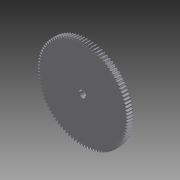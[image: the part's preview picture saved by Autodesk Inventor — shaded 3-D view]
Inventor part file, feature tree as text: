
AUTODESK INVENTOR PART (.ipt)
format: ipt  version: 2013 SP2 (Build 170200200, 200)  size: 855,040 bytes
history: native  units: in
note: dims shown in document units (in); Inventor stores cm internally (conversion verified against a paired STEP export)
features: extrude x4, sketch x4, imported_body x1
ambient origin geometry x8: Origin, YZ Plane, XZ Plane, XY Plane, X Axis, Y Axis, Z Axis, Center Point
bodies: Solid1 (feature_tree)
feature tree (9):
  imported_body  "Base1"
  extrude  "Extrusion2"  Depth=0.66in TaperAngle=0.0deg
  extrude  "Extrusion3"  Depth=0.41in TaperAngle=0.0deg
  extrude  "Extrusion4"  Depth=0.171in
  extrude  "Extrusion5"  Depth=1.0in TaperAngle=0.0deg
  sketch  "Sketch2"  dims[d6=0.215in d7=0.66in d8=0.0in]
  sketch  "Sketch3"  dims[d9=0.7in d11=0.41in d12=0.0in]
  sketch  "Sketch4"  dims[d13=0.15in d14=0.171in]
  sketch  "Sketch5"  dims[d15=0.3in d16=0.0in d19=1.0in d20=0.0in]
